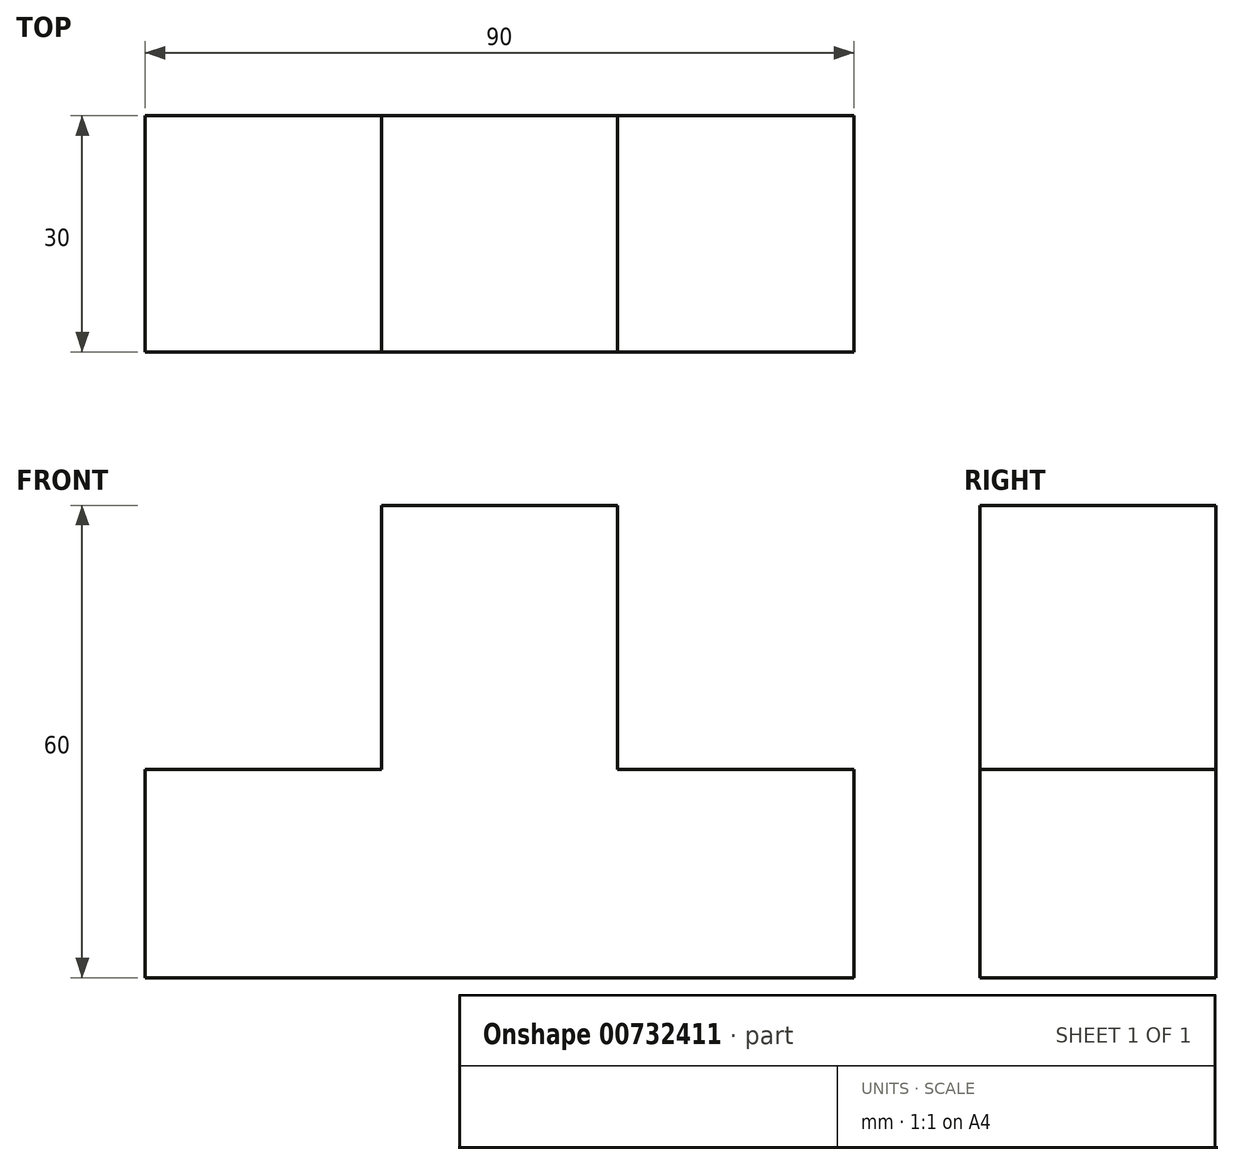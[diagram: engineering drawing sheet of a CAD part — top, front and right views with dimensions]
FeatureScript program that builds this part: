
annotation { "Feature Type Name" : "Feature", "Feature Type Description" : "" }
export const myFeature = defineFeature(function(context is Context, id is Id, definition is map)
    precondition{}
    {
        {
            var Q0;
            Q0=qCreatedBy(makeId("Front.planeOp"),FACE);
            var sketch = newSketch(context, id + "F0", { "sketchPlane" : qUnion([Q0])});
            skLineSegment(sketch, "E0", {"start": v(-42.26, -53.28) * mm, "end": v(47.74, -53.28) * mm});
            skLineSegment(sketch, "E1", {"start": v(47.74, -53.28) * mm, "end": v(47.74, -26.84) * mm});
            skLineSegment(sketch, "E2", {"start": v(47.74, -26.84) * mm, "end": v(17.74, -26.84) * mm});
            skLineSegment(sketch, "E3", {"start": v(17.74, -26.84) * mm, "end": v(17.74, 6.72) * mm});
            skLineSegment(sketch, "E4", {"start": v(17.74, 6.72) * mm, "end": v(-12.26, 6.72) * mm});
            skLineSegment(sketch, "E5", {"start": v(-12.26, 6.72) * mm, "end": v(-12.26, -26.84) * mm});
            skLineSegment(sketch, "E6", {"start": v(-12.26, -26.84) * mm, "end": v(-42.26, -26.84) * mm});
            skLineSegment(sketch, "E7", {"start": v(-42.26, -26.84) * mm, "end": v(-42.26, -53.28) * mm});
            skSolve(sketch);
        }
        {
            var Q0;
            Q0 = qSketchRegion(id + "F0", true);
            extrude(context, id + "F1", {"entities" : qUnion([Q0]), "depth" : 30 * mm, "offsetDistance" : 25 * mm});
        }
    });
